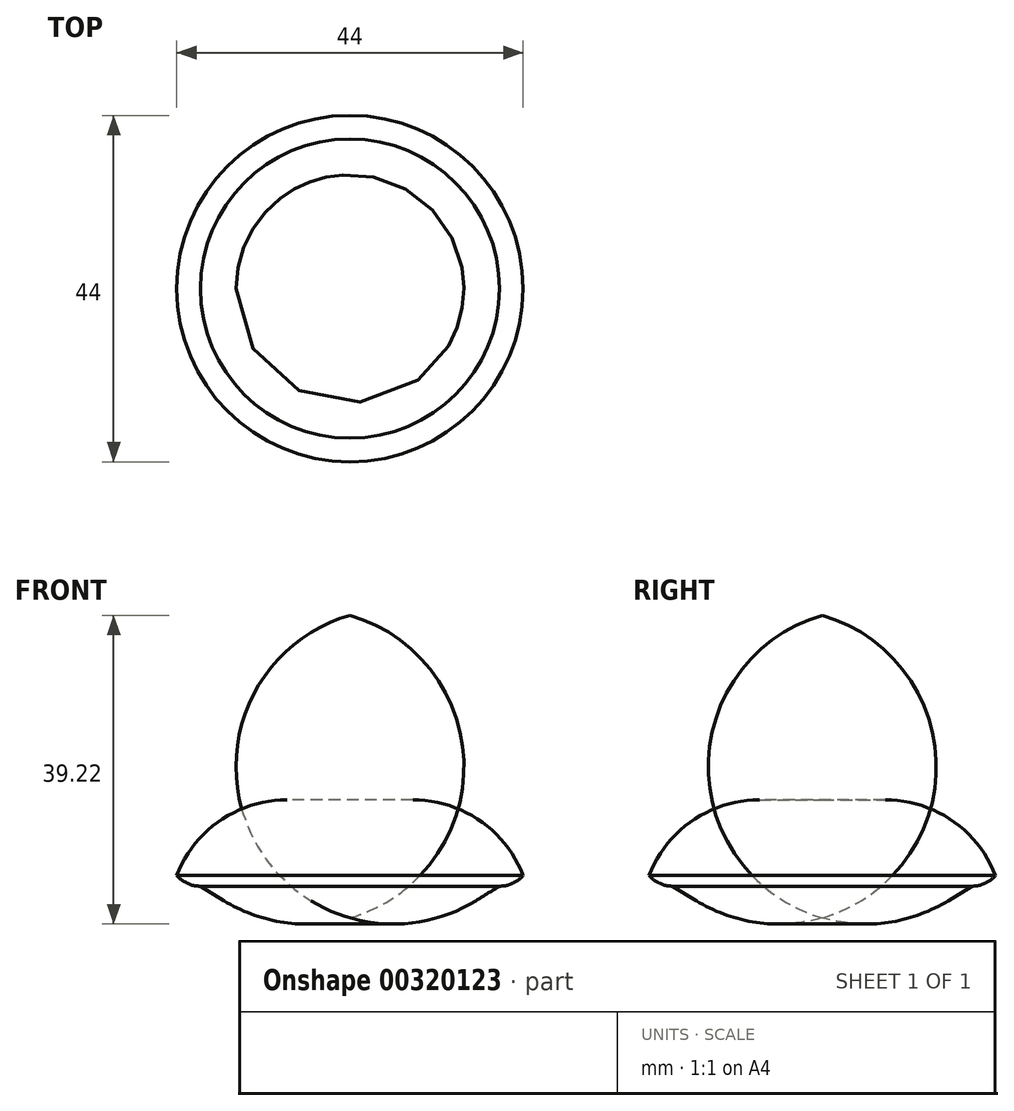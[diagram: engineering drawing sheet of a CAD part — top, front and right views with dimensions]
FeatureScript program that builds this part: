
annotation { "Feature Type Name" : "Feature", "Feature Type Description" : "" }
export const myFeature = defineFeature(function(context is Context, id is Id, definition is map)
    precondition{}
    {
        {
            var Q0;
            Q0=qCreatedBy(makeId("Front.planeOp"),FACE);
            var sketch = newSketch(context, id + "F0", { "sketchPlane" : qUnion([Q0])});
            skLineSegment(sketch, "E0", {"start": v(0, 0) * mm, "end": v(8, 0) * mm});
            skArc(sketch, "E1", {"start": v(22, -9.61) * mm, "mid": v(16.5, -2.64) * mm, "end": v(8, 0) * mm});
            skLineSegment(sketch, "E2", {"start": v(0, 0) * mm, "end": v(0, -15) * mm});
            skArc(sketch, "E3", {"start": v(19, -10.97) * mm, "mid": v(20.65, -10.61) * mm, "end": v(22, -9.61) * mm});
            skLineSegment(sketch, "E4", {"start": v(19, -10.97) * mm, "end": v(0, -10.97) * mm});
            skLineSegment(sketch, "E5", {"start": v(19, -10.97) * mm, "end": v(16, -12.81) * mm});
            skLineSegment(sketch, "E6", {"start": v(16, -12.81) * mm, "end": v(0, -12.81) * mm});
            skArc(sketch, "E7", {"start": v(0, -15) * mm, "mid": v(8.23, -15.6) * mm, "end": v(16, -12.81) * mm});
            skSolve(sketch);
        }
        {
            var Q0;
            {var subQ2=sQuery(id+"F0.wireOp",EDGE,"E6");Q0=makeQuery(id+"F0.imprint","IMPRINT",FACE,{"disambiguationData":[TD([[makeQuery(id+"F0.imprint","IMPRINT",EDGE,{"derivedFrom":subQ2}),1.0]])]});}
            var Q1;
            {var subQ0=sQuery(id+"F0.wireOp",EDGE,"E4");Q1=makeQuery(id+"F0.imprint","IMPRINT",FACE,{"disambiguationData":[TD([[makeQuery(id+"F0.imprint","IMPRINT",EDGE,{"derivedFrom":subQ0}),1.0]])]});}
            var Q2;
            {var subQ1=sQuery(id+"F0.wireOp",EDGE,"E0");Q2=makeQuery(id+"F0.imprint","IMPRINT",FACE,{"disambiguationData":[TD([[makeQuery(id+"F0.imprint","IMPRINT",EDGE,{"derivedFrom":subQ1}),-1.0]])]});}
            var Q3;
            Q3=sQuery(id+"F0.wireOp",EDGE,"E2");
            revolve(context, id + "F1", {"entities" : qUnion([Q0, Q1, Q2]), "axis" : qUnion([Q3]), "revolveType" : RevolveType.FULL});
        }
    });
